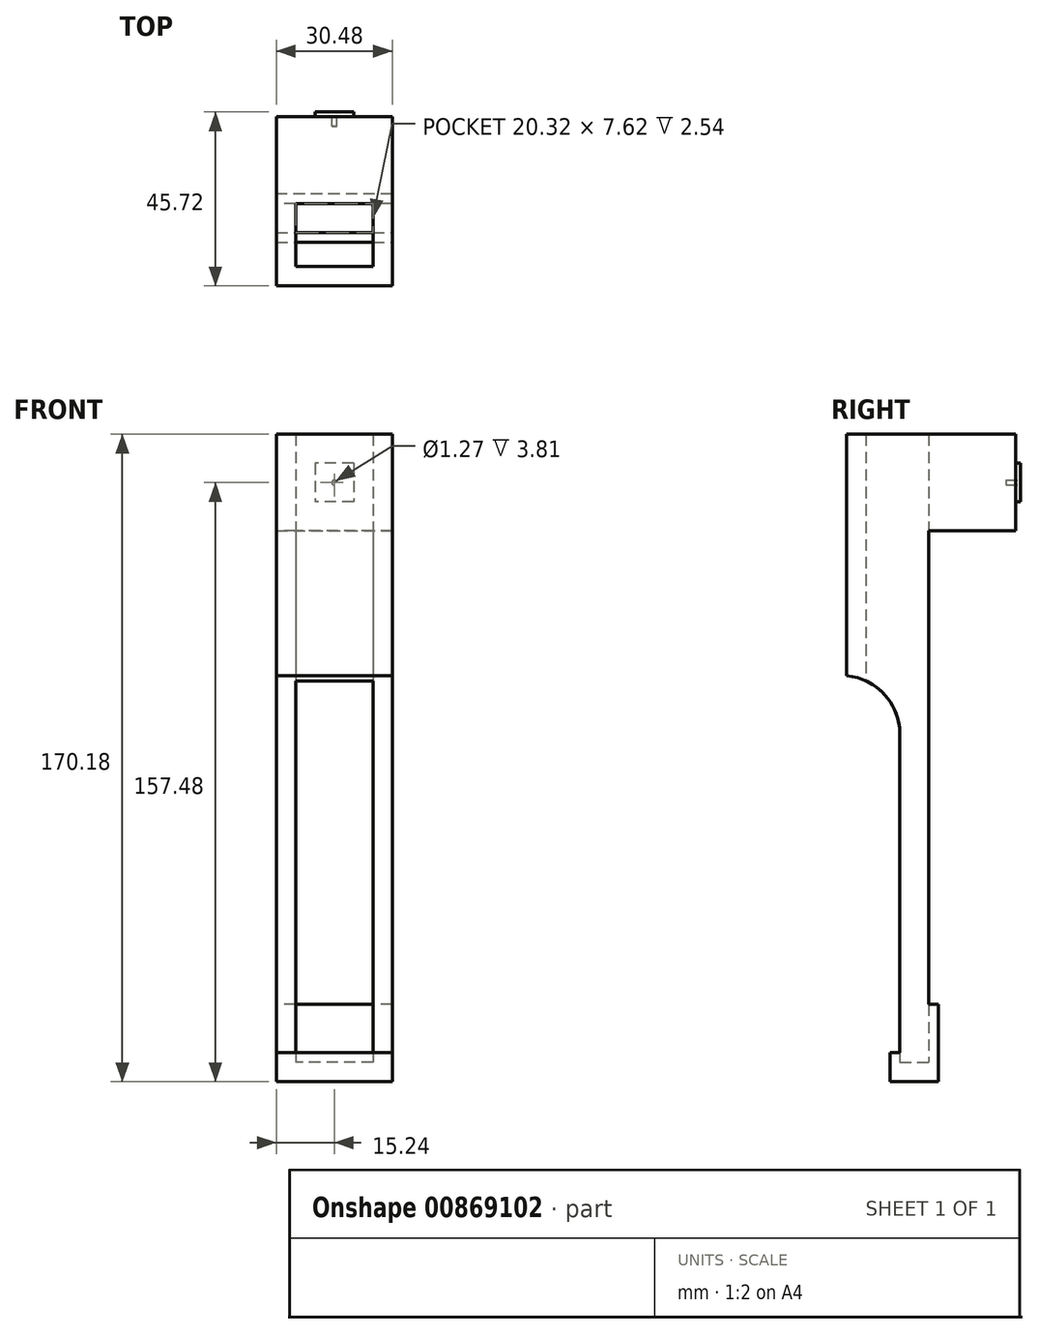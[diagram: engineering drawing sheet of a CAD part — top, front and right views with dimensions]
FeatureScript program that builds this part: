
annotation { "Feature Type Name" : "Feature", "Feature Type Description" : "" }
export const myFeature = defineFeature(function(context is Context, id is Id, definition is map)
    precondition{}
    {
        {
            var Q0;
            Q0=qCreatedBy(makeId("Front.planeOp"),FACE);
            var sketch = newSketch(context, id + "F0", { "sketchPlane" : qUnion([Q0])});
            skLineSegment(sketch, "E0.bottom", {"start": v(15.24, 82.55) * mm, "end": v(10.16, 82.55) * mm});
            skLineSegment(sketch, "E0.top", {"start": v(10.16, -82.55) * mm, "end": v(-10.16, -82.55) * mm});
            skLineSegment(sketch, "E0.left", {"start": v(10.16, 82.55) * mm, "end": v(10.16, -82.55) * mm});
            skLineSegment(sketch, "E0.right", {"start": v(-10.16, 82.55) * mm, "end": v(-10.16, -82.55) * mm});
            skPoint(sketch, "E0.middle", {"position": v(0, 0) * mm});
            skLineSegment(sketch, "E1.2", {"start": v(15.24, 82.55) * mm, "end": v(15.24, -87.63) * mm});
            skLineSegment(sketch, "E1.3", {"start": v(15.24, -87.63) * mm, "end": v(-15.24, -87.63) * mm});
            skLineSegment(sketch, "E2.trimOffspring", {"start": v(-10.16, 82.55) * mm, "end": v(-15.24, 82.55) * mm});
            skLineSegment(sketch, "E3.left", {"start": v(15.24, 82.55) * mm, "end": v(15.24, 6.35) * mm});
            skLineSegment(sketch, "E4", {"start": v(-15.24, 82.55) * mm, "end": v(-15.24, 6.35) * mm});
            skLineSegment(sketch, "E5", {"start": v(-15.24, 6.35) * mm, "end": v(-15.24, -87.63) * mm});
            skSolve(sketch);
        }
        {
            var Q0;
            Q0=makeQuery(id+"F0.imprint","IMPRINT",FACE,{"disambiguationData":[TD([[makeQuery(id+"F0.imprint","IMPRINT",EDGE,{"derivedFrom":sQuery(id+"F0.wireOp",EDGE,"E0.bottom")}),1.0]])]});
            extrude(context, id + "F1", {"entities" : qUnion([Q0]), "depth" : 16.5 * mm, "offsetDistance" : 25.4 * mm});
        }
        {
            var Q0;
            Q0=makeQuery(id+"F1.opExtrude","SWEPT_FACE",FACE,{"disambiguationData":[OSD([sQuery(id+"F0.wireOp",EDGE,"E4"),sQuery(id+"F0.wireOp",EDGE,"E5")])]});
            var sketch = newSketch(context, id + "F2", { "sketchPlane" : qUnion([Q0])});
            skLineSegment(sketch, "E6.bottom", {"start": v(16.51, -87.63) * mm, "end": v(7.62, -87.63) * mm});
            skLineSegment(sketch, "E6.top", {"start": v(16.5, 19.05) * mm, "end": v(7.62, 19.05) * mm});
            skLineSegment(sketch, "E6.left", {"start": v(16.51, -87.63) * mm, "end": v(16.5, 19.05) * mm});
            skLineSegment(sketch, "E6.right", {"start": v(7.62, -87.63) * mm, "end": v(7.62, 19.05) * mm});
            skSolve(sketch);
        }
        {
            var Q0;
            Q0=makeQuery(id+"F2.imprint","IMPRINT",FACE,{"disambiguationData":[TD([[makeQuery(id+"F2.imprint","IMPRINT",EDGE,{"derivedFrom":sQuery(id+"F2.wireOp",EDGE,"E6.bottom")}),-1.0]])]});
            extrude(context, id + "F3", {"entities" : qUnion([Q0]), "operationType" : NewBodyOperationType.REMOVE, "oppositeDirection" : true, "depth" : 50.8 * mm, "offsetDistance" : 25.4 * mm});
        }
        {
            var Q0;
            {var subQ0=sQuery(id+"F0.wireOp",EDGE,"E0.right");var subQ1=sQuery(id+"F0.wireOp",EDGE,"E2.trimOffspring");var subQ2=sQuery(id+"F0.wireOp",EDGE,"E5");var subQ3=sQuery(id+"F0.wireOp",EDGE,"E4");Q0=makeQuery(id+"F3.boolean.opBoolean","SPLIT",FACE,{"disambiguationData":[TD([makeQuery(id+"F1.opExtrude","SWEPT_FACE",FACE,{"disambiguationData":[OSD([subQ0])]})])],"derivedFrom":makeQuery(id+"F1.opExtrude","CAP_FACE",FACE,{"disambiguationData":[OSD([sQuery(id+"F0.wireOp",EDGE,"E0.bottom"),sQuery(id+"F0.wireOp",EDGE,"E0.top"),sQuery(id+"F0.wireOp",EDGE,"E0.left"),subQ0,sQuery(id+"F0.wireOp",EDGE,"E1.2"),sQuery(id+"F0.wireOp",EDGE,"E1.3"),subQ1,sQuery(id+"F0.wireOp",EDGE,"E3.left"),subQ3,subQ2])],"isStart":false})});}
            var sketch = newSketch(context, id + "F4", { "sketchPlane" : qUnion([Q0])});
            skLineSegment(sketch, "E7.bottom", {"start": v(-15.24, 82.55) * mm, "end": v(15.24, 82.55) * mm});
            skLineSegment(sketch, "E7.top", {"start": v(-15.24, 19.05) * mm, "end": v(15.24, 19.05) * mm});
            skLineSegment(sketch, "E7.left", {"start": v(-15.24, 82.55) * mm, "end": v(-15.24, 19.05) * mm});
            skLineSegment(sketch, "E7.right", {"start": v(15.24, 82.55) * mm, "end": v(15.24, 19.05) * mm});
            skSolve(sketch);
        }
        {
            var Q0;
            {var subQ2=sQuery(id+"F4.wireOp",EDGE,"E7.left");Q0=makeQuery(id+"F4.imprint","IMPRINT",FACE,{"disambiguationData":[TD([[makeQuery(id+"F4.imprint","IMPRINT",EDGE,{"derivedFrom":subQ2}),1.0]])]});}
            var Q1;
            {var subQ2=sQuery(id+"F4.wireOp",EDGE,"E7.right");Q1=makeQuery(id+"F4.imprint","IMPRINT",FACE,{"disambiguationData":[TD([[makeQuery(id+"F4.imprint","IMPRINT",EDGE,{"derivedFrom":subQ2}),-1.0]])]});}
            extrude(context, id + "F5", {"entities" : qUnion([Q0, Q1]), "operationType" : NewBodyOperationType.ADD, "depth" : 5.08 * mm, "offsetDistance" : 25.4 * mm});
        }
        {
            var Q0;
            {var subQ0=sQuery(id+"F2.wireOp",EDGE,"E6.top");var subQ1=sQuery(id+"F2.wireOp",EDGE,"E6.right");Q0=makeQuery(id+"F3.boolean.opBoolean","COPY",EDGE,{"disambiguationData":[TD([makeQuery(id+"F1.opExtrude","SWEPT_FACE",FACE,{"disambiguationData":[OSD([sQuery(id+"F0.wireOp",EDGE,"E0.right")])]})])],"derivedFrom":makeQuery(id+"F3.opExtrude","SWEPT_EDGE",EDGE,{"disambiguationData":[OSD([subQ0,subQ1])]})});}
            fillet(context, id + "F6", {"entities" : qUnion([Q0]), "radius" : 15.24 * mm, "tangentPropagation" : true, "allowEdgeOverflow" : false});
        }
        {
            var Q0;
            Q0=makeQuery(id+"F5.boolean.opBoolean","MERGE",FACE,{"derivedFrom":[makeQuery(id+"F1.opExtrude","SWEPT_FACE",FACE,{"disambiguationData":[OSD([sQuery(id+"F0.wireOp",EDGE,"E0.bottom")])]}),makeQuery(id+"F1.opExtrude","SWEPT_FACE",FACE,{"disambiguationData":[OSD([sQuery(id+"F0.wireOp",EDGE,"E2.trimOffspring")])]}),makeQuery(id+"F5.opExtrude","SWEPT_FACE",FACE,{"disambiguationData":[OSD([sQuery(id+"F4.wireOp",EDGE,"E7.bottom")])]})]});
            var sketch = newSketch(context, id + "F7", { "sketchPlane" : qUnion([Q0])});
            skLineSegment(sketch, "E8.bottom", {"start": v(15.24, -21.6) * mm, "end": v(45.72, -21.6) * mm});
            skLineSegment(sketch, "E8.top", {"start": v(15.24, 22.86) * mm, "end": v(45.72, 22.86) * mm});
            skLineSegment(sketch, "E8.left", {"start": v(15.24, -21.6) * mm, "end": v(15.24, 0) * mm});
            skLineSegment(sketch, "E8.right", {"start": v(45.72, -21.6) * mm, "end": v(45.72, 22.86) * mm});
            skLineSegment(sketch, "E9", {"start": v(0, -16.51) * mm, "end": v(0, -21.6) * mm});
            skCircle(sketch, "E10", {"center": v(33.02, 11.43) * mm, "radius": 1.27 * mm});
            skLineSegment(sketch, "E11.MirrorCS", {"start": v(-15.24, -21.59) * mm, "end": v(-15.24, 0) * mm});
            skLineSegment(sketch, "E12.MirrorCS", {"start": v(-15.24, 22.86) * mm, "end": v(-45.72, 22.86) * mm});
            skLineSegment(sketch, "E13.MirrorCS", {"start": v(-45.72, -21.6) * mm, "end": v(-45.72, 22.86) * mm});
            skCircle(sketch, "E14.MirrorC", {"center": v(-33.02, 11.43) * mm, "radius": 1.27 * mm});
            skLineSegment(sketch, "E15.MirrorCS", {"start": v(-15.24, -21.6) * mm, "end": v(-45.72, -21.6) * mm});
            skLineSegment(sketch, "E16.bottom", {"start": v(15.24, 0) * mm, "end": v(15.24, 0) * mm});
            skLineSegment(sketch, "E16.right", {"start": v(15.24, 0) * mm, "end": v(15.24, 22.86) * mm});
            skLineSegment(sketch, "E17.MirrorCS", {"start": v(-15.24, 0) * mm, "end": v(-15.24, 22.86) * mm});
            skLineSegment(sketch, "E18.MirrorCS", {"start": v(-15.24, 0) * mm, "end": v(-15.24, 0) * mm});
            skPoint(sketch, "E19.orphan", {"position": v(15.24, 22.86) * mm});
            skPoint(sketch, "E20.orphan", {"position": v(-15.24, 22.86) * mm});
            skLineSegment(sketch, "E21.bottom", {"start": v(-15.24, 0) * mm, "end": v(15.24, 0) * mm});
            skLineSegment(sketch, "E21.top", {"start": v(-15.24, 22.86) * mm, "end": v(15.24, 22.86) * mm});
            skSolve(sketch);
        }
        {
            var Q0;
            Q0=makeQuery(id+"F7.imprint","IMPRINT",FACE,{"disambiguationData":[TD([[makeQuery(id+"F7.imprint","IMPRINT",EDGE,{"derivedFrom":sQuery(id+"F7.wireOp",EDGE,"E21.top")}),-1.0]])]});
            extrude(context, id + "F8", {"entities" : qUnion([Q0]), "operationType" : NewBodyOperationType.ADD, "oppositeDirection" : true, "depth" : 25.4 * mm, "offsetDistance" : 25.4 * mm});
        }
        {
            var Q0;
            Q0=makeQuery(id+"F1.opExtrude","CAP_FACE",FACE,{"disambiguationData":[OSD([sQuery(id+"F0.wireOp",EDGE,"E0.bottom"),sQuery(id+"F0.wireOp",EDGE,"E0.top"),sQuery(id+"F0.wireOp",EDGE,"E0.left"),sQuery(id+"F0.wireOp",EDGE,"E0.right"),sQuery(id+"F0.wireOp",EDGE,"E1.2"),sQuery(id+"F0.wireOp",EDGE,"E1.3"),sQuery(id+"F0.wireOp",EDGE,"E2.trimOffspring"),sQuery(id+"F0.wireOp",EDGE,"E3.left"),sQuery(id+"F0.wireOp",EDGE,"E4"),sQuery(id+"F0.wireOp",EDGE,"E5")])],"isStart":true});
            var sketch = newSketch(context, id + "F9", { "sketchPlane" : qUnion([Q0])});
            skLineSegment(sketch, "E22.bottom", {"start": v(-15.24, -87.63) * mm, "end": v(15.24, -87.63) * mm});
            skLineSegment(sketch, "E22.top", {"start": v(-15.24, -67.3) * mm, "end": v(15.24, -67.3) * mm});
            skLineSegment(sketch, "E22.left", {"start": v(-15.24, -87.63) * mm, "end": v(-15.24, -67.3) * mm});
            skLineSegment(sketch, "E22.right", {"start": v(15.24, -87.63) * mm, "end": v(15.24, -67.3) * mm});
            skSolve(sketch);
        }
        {
            var Q0;
            Q0=makeQuery(id+"F9.imprint","IMPRINT",FACE,{"disambiguationData":[TD([[makeQuery(id+"F9.imprint","IMPRINT",EDGE,{"derivedFrom":sQuery(id+"F9.wireOp",EDGE,"E22.bottom")}),1.0]])]});
            var Q1;
            {var subQ3=sQuery(id+"F0.wireOp",EDGE,"E0.top");var subQ9=makeQuery(id+"F1.opExtrude","CAP_EDGE",EDGE,{"disambiguationData":[OSD([subQ3])],"isStart":true});Q1=makeQuery(id+"F9.imprint","IMPRINT",FACE,{"disambiguationData":[TD([[makeQuery(id+"F9.imprint","IMPRINT",EDGE,{"derivedFrom":subQ9}),1.0]])]});}
            extrude(context, id + "F10", {"entities" : qUnion([Q0, Q1]), "operationType" : NewBodyOperationType.ADD, "depth" : 2.54 * mm, "offsetDistance" : 25.4 * mm});
        }
        {
            var Q0;
            Q0=makeQuery(id+"F3.boolean.opBoolean","COPY",FACE,{"derivedFrom":makeQuery(id+"F3.opExtrude","SWEPT_FACE",FACE,{"disambiguationData":[OSD([sQuery(id+"F2.wireOp",EDGE,"E6.right")])]})});
            var sketch = newSketch(context, id + "F11", { "sketchPlane" : qUnion([Q0])});
            skLineSegment(sketch, "E23.bottom", {"start": v(-15.24, -87.63) * mm, "end": v(15.24, -87.63) * mm});
            skLineSegment(sketch, "E23.top", {"start": v(-15.24, -80) * mm, "end": v(15.24, -80) * mm});
            skLineSegment(sketch, "E23.left", {"start": v(-15.24, -87.63) * mm, "end": v(-15.24, -80) * mm});
            skLineSegment(sketch, "E23.right", {"start": v(15.24, -87.63) * mm, "end": v(15.24, -80) * mm});
            skSolve(sketch);
        }
        {
            var Q0;
            {var subQ1=makeQuery(id+"F3.opExtrude","SWEPT_FACE",FACE,{"disambiguationData":[OSD([sQuery(id+"F2.wireOp",EDGE,"E6.right")])]});var subQ6=makeQuery(id+"F3.boolean.opBoolean","INTERSECT",EDGE,{"derivedFrom":[makeQuery(id+"F1.opExtrude","SWEPT_FACE",FACE,{"disambiguationData":[OSD([sQuery(id+"F0.wireOp",EDGE,"E0.top")])]}),subQ1]});Q0=makeQuery(id+"F11.imprint","IMPRINT",FACE,{"disambiguationData":[TD([[makeQuery(id+"F11.imprint","IMPRINT",EDGE,{"derivedFrom":subQ6}),-1.0]])]});}
            var Q1;
            Q1=makeQuery(id+"F11.imprint","IMPRINT",FACE,{"disambiguationData":[TD([[makeQuery(id+"F11.imprint","IMPRINT",EDGE,{"derivedFrom":sQuery(id+"F11.wireOp",EDGE,"E23.bottom")}),-1.0]])]});
            extrude(context, id + "F12", {"entities" : qUnion([Q0, Q1]), "operationType" : NewBodyOperationType.ADD, "depth" : 2.54 * mm, "offsetDistance" : 25.4 * mm});
        }
        {
            var Q0;
            Q0=makeQuery(id+"F8.opExtrude","SWEPT_FACE",FACE,{"disambiguationData":[OSD([sQuery(id+"F7.wireOp",EDGE,"E21.top")])]});
            var sketch = newSketch(context, id + "F13", { "sketchPlane" : qUnion([Q0])});
            skCircle(sketch, "E24", {"center": v(0, 69.85) * mm, "radius": 0.64 * mm});
            skSolve(sketch);
        }
        {
            var Q0;
            Q0=makeQuery(id+"F13.imprint","IMPRINT",FACE,{"disambiguationData":[TD([[makeQuery(id+"F13.imprint","IMPRINT",EDGE,{"derivedFrom":sQuery(id+"F13.wireOp",EDGE,"E24")}),1.0]])]});
            extrude(context, id + "F14", {"entities" : qUnion([Q0]), "operationType" : NewBodyOperationType.REMOVE, "oppositeDirection" : true, "depth" : 2.54 * mm, "offsetDistance" : 25.4 * mm});
        }
        {
            var Q0;
            Q0=makeQuery(id+"F8.opExtrude","SWEPT_FACE",FACE,{"disambiguationData":[OSD([sQuery(id+"F7.wireOp",EDGE,"E21.top")])]});
            var sketch = newSketch(context, id + "F15", { "sketchPlane" : qUnion([Q0])});
            skLineSegment(sketch, "E25.bottom", {"start": v(-5.08, 74.93) * mm, "end": v(5.08, 74.93) * mm});
            skLineSegment(sketch, "E25.top", {"start": v(-5.08, 64.77) * mm, "end": v(5.08, 64.77) * mm});
            skLineSegment(sketch, "E25.left", {"start": v(-5.08, 74.93) * mm, "end": v(-5.08, 64.77) * mm});
            skLineSegment(sketch, "E25.right", {"start": v(5.08, 74.93) * mm, "end": v(5.08, 64.77) * mm});
            skPoint(sketch, "E25.middle", {"position": v(0, 69.85) * mm});
            skSolve(sketch);
        }
        {
            var Q0;
            Q0=makeQuery(id+"F15.imprint","IMPRINT",FACE,{"disambiguationData":[TD([[makeQuery(id+"F15.imprint","IMPRINT",EDGE,{"derivedFrom":sQuery(id+"F15.wireOp",EDGE,"E25.bottom")}),-1.0]])]});
            extrude(context, id + "F16", {"entities" : qUnion([Q0]), "operationType" : NewBodyOperationType.ADD, "depth" : 1.27 * mm, "offsetDistance" : 25.4 * mm});
        }
    });
